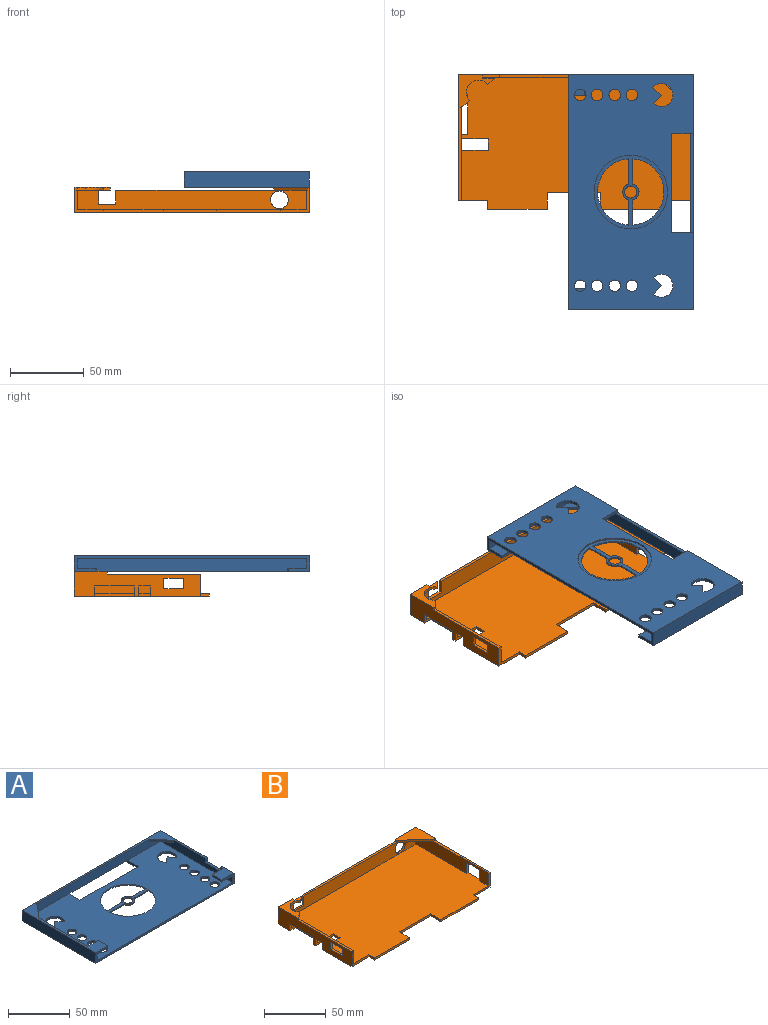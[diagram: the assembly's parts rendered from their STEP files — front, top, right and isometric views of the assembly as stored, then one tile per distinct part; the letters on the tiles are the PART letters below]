
ASSEMBLY  parts=2 mates=1
PART A: 53 faces, bbox 159x84.7x10.6 mm
  f0: plane 159x84.65mm, normal (0,0,-1), area 9869.2mm2, adj f2,f17,f18,f19,f24,f25,f26,f28
  f1: plane 155x82.65mm, normal (0,0,1), area 9857mm2, adj f4,f10,f11,f18,f24,f25,f26,f28
  f2: plane 159x10.6mm, normal (0,1,0), area 1551.4mm2, adj f0,f17,f19,f20,f24,f25,f27
  f3: plane 14x13.9mm, normal (0,0,1), area 159.8mm2, adj f4,f6,f16,f18,f19,f22
  f4: plane 82.65x8.6mm, normal (-1,0,0), area 589.2mm2, adj f1,f3,f7,f10,f12,f13,f16,f18
  f5: plane 11x2mm, normal (1,0,0), area 22mm2, adj f9,f15,f18,f20
  f6: plane 11x2mm, normal (-1,0,0), area 22mm2, adj f3,f12,f16,f18
  f7: plane 15.67x13mm, normal (0,0,-1), area 101.9mm2, adj f4,f10,f13
  f8: plane 15.67x13mm, normal (0,0,-1), area 101.9mm2, adj f10,f11,f14
  f9: plane 12x11mm, normal (0,0,-1), area 132mm2, adj f5,f11,f15,f18
  f10: plane 155x8.6mm, normal (0,-1,0), area 1281mm2, adj f1,f4,f7,f8,f11,f13,f14,f20
  f11: plane 82.65x8.6mm, normal (1,0,0), area 657.4mm2, adj f1,f8,f9,f10,f14,f15,f18,f20
  f12: plane 12x11mm, normal (0,0,-1), area 132mm2, adj f4,f6,f16,f18
  f13: plane 15.67x13mm, normal (-0.77,-0.64,0), area 40.7mm2, adj f4,f7,f10,f20
  f14: plane 15.67x13mm, normal (0.77,-0.64,0), area 40.7mm2, adj f8,f10,f11,f20
  f15: plane 12x2mm, normal (0,1,0), area 24mm2, adj f5,f9,f11,f20
  f16: plane 12x2mm, normal (0,1,0), area 24mm2, adj f3,f4,f6,f12
  f17: plane 84.65x10.6mm, normal (-1,0,0), area 897.3mm2, adj f0,f2,f18,f20
  f18: plane 159x10.6mm, normal (0,-1,0), area 400.4mm2, adj f0,f1,f3,f4,f5,f6,f9,f11
  f19: plane 84.65x10.6mm, normal (1,0,0), area 829.1mm2, adj f0,f2,f3,f18,f20,f21,f22,f23
  f20: plane 159x84.65mm, normal (0,0,1), area 922.4mm2, adj f2,f4,f5,f10,f11,f13,f14,f15
  f21: plane 4x2mm, normal (0,-1,0), area 8mm2, adj f4,f19,f20,f23
  f22: plane 4x2mm, normal (0,1,0), area 8mm2, adj f3,f4,f19,f23
  f23: plane 17.05x2mm, normal (0,0,1), area 34.1mm2, adj f4,f19,f21,f22
  f24: plane 14.54x2mm, normal (1,0,0), area 29.1mm2, adj f0,f1,f2,f26,f27
  f25: plane 14.54x2mm, normal (-1,0,0), area 29.1mm2, adj f0,f1,f2,f26,f27
  f26: plane 67x2mm, normal (0,1,0), area 134mm2, adj f0,f1,f24,f25
  f27: plane 67x2mm, normal (0,0,-1), area 134mm2, adj f2,f10,f24,f25
  f28: cylinder r=7.79mm len=15.57mm, axis (0,0,-1), area 73.4mm2, adj f0,f1,f29,f30
  f29: plane 5.65x5.36mm, normal (0.73,0.69,0), area 15.6mm2, adj f0,f1,f28,f30
  f30: plane 5.65x5.36mm, normal (-0.69,0.73,0), area 15.6mm2, adj f0,f1,f28,f29
  f31: cylinder r=5.57mm len=10.8mm, axis (0,0,-1), area 14.7mm2, adj f1,f32,f34,f52
  f32: plane 17.02x1mm, normal (0,1,0), area 17mm2, adj f1,f31,f33,f52
  f33: cylinder r=22.46mm len=44.83mm, axis (0,0,-1), area 67.8mm2, adj f1,f32,f34,f52
  f34: plane 17.02x1mm, normal (0,1,0), area 17mm2, adj f1,f31,f33,f52
  f35: cylinder r=5.57mm len=10.79mm, axis (0,0,-1), area 14.7mm2, adj f1,f36,f38,f52
  f36: plane 17.02x1mm, normal (0,-1,0), area 17mm2, adj f1,f35,f37,f52
  f37: cylinder r=22.46mm len=44.83mm, axis (0,0,-1), area 67.7mm2, adj f1,f36,f38,f52
  f38: plane 17.02x1mm, normal (0,-1,0), area 17mm2, adj f1,f35,f37,f52
  f39: cylinder r=7.79mm len=15.57mm, axis (0,0,-1), area 73.4mm2, adj f0,f1,f40,f41
  f40: plane 5.96x5.02mm, normal (0.76,0.64,0), area 15.6mm2, adj f0,f1,f39,f41
  f41: plane 5.96x5.02mm, normal (-0.64,0.76,0), area 15.6mm2, adj f0,f1,f39,f40
  f42: cylinder r=3.91mm len=7.81mm, axis (0,0,-1), area 49.1mm2, adj f0,f1
  f43: cylinder r=4.08mm len=8.16mm, axis (0,0,-1), area 25.6mm2, adj f1,f52
  f44: cylinder r=3.91mm len=7.81mm, axis (0,0,-1), area 49.1mm2, adj f0,f1
  f45: cylinder r=3.91mm len=7.81mm, axis (0,0,-1), area 49.1mm2, adj f0,f1
  f46: cylinder r=3.91mm len=7.81mm, axis (0,0,-1), area 49.1mm2, adj f0,f1
  f47: cylinder r=3.91mm len=7.81mm, axis (0,0,-1), area 49.1mm2, adj f0,f1
  f48: cylinder r=3.91mm len=7.81mm, axis (0,0,-1), area 49.1mm2, adj f0,f1
  f49: cylinder r=3.91mm len=7.81mm, axis (0,0,-1), area 49.1mm2, adj f0,f1
  f50: cylinder r=3.91mm len=7.81mm, axis (0,0,-1), area 49.1mm2, adj f0,f1
  f51: cylinder r=24.9mm len=49.79mm, axis (0,0,-1), area 156.4mm2, adj f0,f52
  f52: plane 49.79x49.79mm, normal (0,0,-1), area 502.5mm2, adj f31,f32,f33,f34,f35,f36,f37,f38
PART B: 51 faces, bbox 158.7x91.3x16.9 mm
  f0: plane 85.1x16.9mm, normal (-1,0,0), area 973.1mm2, adj f3,f8,f10,f15,f27,f28,f38,f39
  f1: plane 83.1x14.9mm, normal (1,0,0), area 802.9mm2, adj f2,f8,f9,f11,f15,f19,f27,f28
  f2: plane 156.66x89.3mm, normal (0,0,1), area 12961.8mm2, adj f1,f4,f5,f6,f7,f9,f13,f14
  f3: plane 158.66x91.3mm, normal (0,0,-1), area 13512.6mm2, adj f0,f4,f5,f6,f7,f10,f13,f14
  f4: plane 6.2x2mm, normal (1,0,0), area 12.4mm2, adj f2,f3,f14,f37
  f5: plane 6.2x2mm, normal (-1,0,0), area 12.4mm2, adj f2,f3,f15,f36
  f6: plane 11.44x2mm, normal (-1,0,0), area 22.9mm2, adj f2,f3,f35,f37
  f7: plane 11.44x2mm, normal (1,0,0), area 22.9mm2, adj f2,f3,f35,f36
  f8: plane 24.17x22.12mm, normal (0,0,1), area 189.6mm2, adj f0,f1,f10,f12,f19,f27,f31,f32
  f9: plane 154.66x12.9mm, normal (0,-1,0), area 1773.1mm2, adj f1,f2,f11,f16,f18,f26,f30,f31
  f10: plane 158.66x16.9mm, normal (0,1,0), area 2222.5mm2, adj f0,f3,f8,f13,f17,f25,f26,f30
  f11: plane 22.17x19.97mm, normal (0,0,-1), area 117mm2, adj f1,f9,f12,f19,f31,f32,f50
  f12: plane 4.55x3.98mm, normal (0.66,-0.75,0), area 12.1mm2, adj f8,f11,f32,f50
  f13: plane 85.1x16.9mm, normal (1,0,0), area 1151.3mm2, adj f2,f3,f10,f14,f17,f21,f22,f23
  f14: plane 19.5x14.9mm, normal (0,-1,0), area 64.8mm2, adj f2,f3,f4,f13,f16,f21
  f15: plane 19.5x14.9mm, normal (0,-1,0), area 64.8mm2, adj f0,f1,f2,f3,f5,f28
  f16: plane 83.1x12.9mm, normal (-1,0,0), area 911.4mm2, adj f2,f9,f14,f18,f21,f22,f23,f24
  f17: plane 24.08x21.97mm, normal (0,0,1), area 300.8mm2, adj f10,f13,f20,f25,f29
  f18: plane 22.08x19.3mm, normal (0,0,-1), area 213mm2, adj f9,f16,f20
  f19: plane 5.24x4.58mm, normal (0.66,-0.75,0), area 13.9mm2, adj f1,f8,f11,f50
  f20: plane 22.85x19.97mm, normal (-0.66,-0.75,0), area 60.7mm2, adj f17,f18,f21,f25,f29
  f21: plane 63.8x2mm, normal (0,0,1), area 126.5mm2, adj f13,f14,f16,f20,f29
  f22: plane 14.6x2mm, normal (0,0,-1), area 29.2mm2, adj f13,f16,f23,f24
  f23: plane 11x2mm, normal (0,1,0), area 22mm2, adj f2,f13,f16,f22
  f24: plane 11x2mm, normal (0,-1,0), area 22mm2, adj f2,f13,f16,f22
  f25: plane 2x2mm, normal (-1,0,0), area 4mm2, adj f10,f17,f20,f26
  f26: plane 106.83x2mm, normal (0,0,1), area 213.7mm2, adj f9,f10,f25,f33
  f27: plane 2x2mm, normal (0,-1,0), area 4mm2, adj f0,f1,f8,f28
  f28: plane 62.98x2mm, normal (0,0,1), area 126mm2, adj f0,f1,f15,f27
  f29: plane 2x1.23mm, normal (0,-1,0), area 2.5mm2, adj f13,f17,f20,f21
  f30: plane 11.6x2mm, normal (0,0,1), area 23.2mm2, adj f9,f10,f31,f33
  f31: plane 11.39x2.6mm, normal (1,0,0), area 24mm2, adj f8,f9,f10,f11,f30,f32
  f32: plane 8.01x2mm, normal (0,1,0), area 16mm2, adj f8,f11,f12,f31
  f33: plane 9.39x2mm, normal (-1,0,0), area 18.8mm2, adj f9,f10,f26,f30
  f34: cylinder r=6mm len=12mm, axis (0,1,0), area 75.4mm2, adj f9,f10
  f35: plane 36x2mm, normal (0,-1,0), area 72mm2, adj f2,f3,f6,f7
  f36: plane 40.36x2mm, normal (0,-1,0), area 80.7mm2, adj f2,f3,f5,f7
  f37: plane 43.3x2mm, normal (0,-1,0), area 86.6mm2, adj f2,f3,f4,f6
  f38: plane 27x2mm, normal (0,0,-1), area 54mm2, adj f0,f1,f39,f40
  f39: plane 7x6mm, normal (0,1,0), area 22mm2, adj f0,f1,f2,f3,f38,f41
  f40: plane 7x6mm, normal (0,-1,0), area 22mm2, adj f0,f1,f2,f3,f38,f41
  f41: plane 27x2mm, normal (-1,0,0), area 54mm2, adj f2,f3,f39,f40
  f42: plane 7.85x2mm, normal (0,0,-1), area 15.7mm2, adj f0,f1,f43,f44
  f43: plane 20x7mm, normal (0,1,0), area 50mm2, adj f0,f1,f2,f3,f42,f45
  f44: plane 20x7mm, normal (0,-1,0), area 50mm2, adj f0,f1,f2,f3,f42,f45
  f45: plane 7.85x2mm, normal (-1,0,0), area 15.7mm2, adj f2,f3,f43,f44
  f46: plane 13.5x2mm, normal (0,0,-1), area 27mm2, adj f0,f1,f47,f49
  f47: plane 7.05x2mm, normal (0,-1,0), area 14.1mm2, adj f0,f1,f46,f48
  f48: plane 13.5x2mm, normal (0,0,1), area 27mm2, adj f0,f1,f47,f49
  f49: plane 7.05x2mm, normal (0,1,0), area 14.1mm2, adj f0,f1,f46,f48
  f50: cylinder r=8.22mm len=14.41mm, axis (0,0,1), area 51.7mm2, adj f8,f11,f12,f19
PLACE A rot(axis=(0.71,0.71,0),180deg) t=(-6.6,-85.4,14.49)mm
PLACE B t=(-19.21,-26.65,-9.01)mm fixed
MATE fastened A.f20 <-> B.f17  axis (0,0,-1) through (61.59,33.7,5.89)mm
